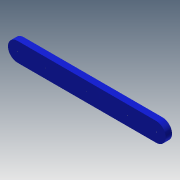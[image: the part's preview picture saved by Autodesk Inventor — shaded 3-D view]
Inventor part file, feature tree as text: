
AUTODESK INVENTOR PART (.ipt)
format: ipt  version: 2013 (Build 170138000, 138)  size: 130,560 bytes
history: native  units: mm
features: extrude x7, sketch x7
ambient origin geometry x8: Origin, YZ Plane, XZ Plane, XY Plane, X Axis, Y Axis, Z Axis, Center Point
bodies: Solid1 (feature_tree)
feature tree (14):
  extrude  "Extrusion1"  Depth=6.0mm
  extrude  "Extrusion2"  Depth=6.0mm
  extrude  "Extrusion3"  Depth=3.0mm
  extrude  "Extrusion4"  Depth=3.0mm
  extrude  "Extrusion5"  Depth=10.0mm
  extrude  "Extrusion6"  Depth=2.0mm TaperAngle=0.0deg
  extrude  "Extrusion7"  Depth=0.2mm
  sketch  "Sketch1"  dims[d0=44.0mm d1=6.0mm]
  sketch  "Sketch2"  dims[d2=6.0mm d3=6.0mm]
  sketch  "Sketch3"  dims[d4=2.0mm d5=0.0mm d6=3.0mm]
  sketch  "Sketch4"  dims[d7=3.0mm d8=3.0mm]
  sketch  "Sketch5"  dims[d9=2.0mm d10=0.0mm d11=10.0mm]
  sketch  "Sketch6"  dims[d12=3.0mm d13=2.0mm d14=0.0mm]
  sketch  "Sketch7"  dims[d15=0.2mm d16=0.2mm d17=0.2mm d18=0.2mm d19=2.0mm d20=0.0mm d21=0.2mm d22=2.0mm d23=0.0mm d24=12.985mm d25=0.2mm d26=12.985mm d27=0.2mm d28=2.0mm d29=0.0mm d30=2.0mm d31=0.0mm]
